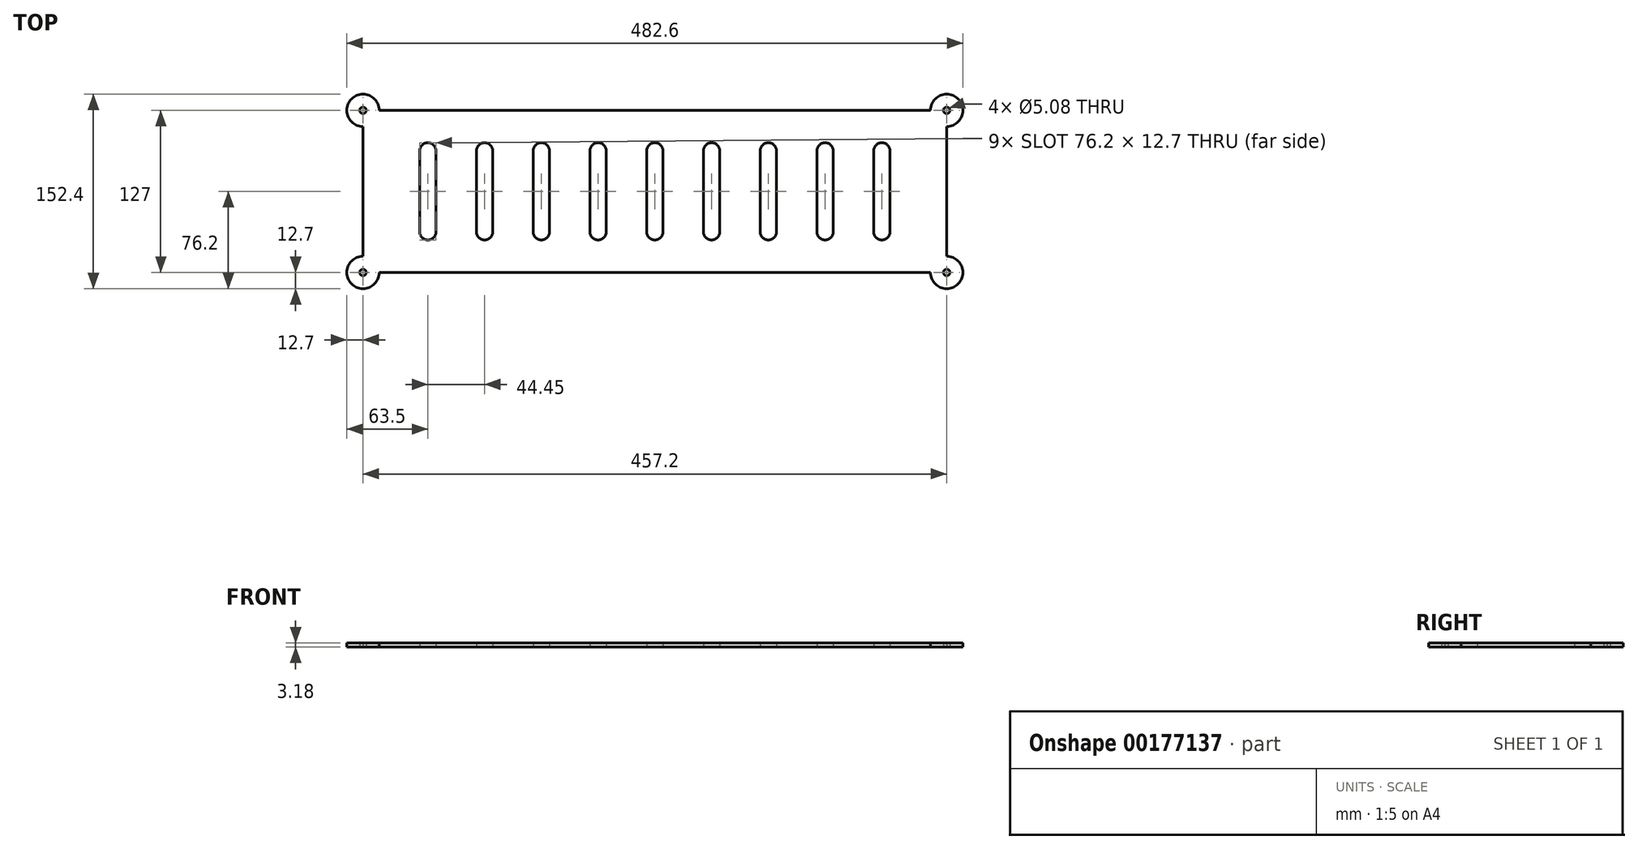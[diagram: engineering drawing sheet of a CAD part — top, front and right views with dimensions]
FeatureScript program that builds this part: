
annotation { "Feature Type Name" : "Feature", "Feature Type Description" : "" }
export const myFeature = defineFeature(function(context is Context, id is Id, definition is map)
    precondition{}
    {
        {
            var Q0;
            Q0=qCreatedBy(makeId("Top.planeOp"),FACE);
            var sketch = newSketch(context, id + "F0", { "sketchPlane" : qUnion([Q0])});
            skLineSegment(sketch, "E0.bottom", {"start": v(12.7, 0) * mm, "end": v(444.5, 0) * mm});
            skLineSegment(sketch, "E0.top", {"start": v(12.7, 127) * mm, "end": v(444.5, 127) * mm});
            skLineSegment(sketch, "E0.left", {"start": v(0, 12.7) * mm, "end": v(0, 114.3) * mm});
            skLineSegment(sketch, "E0.right", {"start": v(457.2, 12.7) * mm, "end": v(457.2, 114.3) * mm});
            skArc(sketch, "E1", {"start": v(457.2, 114.3) * mm, "mid": v(466.18, 135.98) * mm, "end": v(444.5, 127) * mm});
            skArc(sketch, "E2", {"start": v(444.5, 0) * mm, "mid": v(466.18, -8.98) * mm, "end": v(457.2, 12.7) * mm});
            skArc(sketch, "E3", {"start": v(0, 12.7) * mm, "mid": v(-8.98, -8.98) * mm, "end": v(12.7, 0) * mm});
            skArc(sketch, "E4", {"start": v(12.7, 127) * mm, "mid": v(-8.98, 135.98) * mm, "end": v(0, 114.3) * mm});
            skCircle(sketch, "E5", {"center": v(0, 127) * mm, "radius": 2.54 * mm});
            skCircle(sketch, "E6", {"center": v(0, 0) * mm, "radius": 2.54 * mm});
            skCircle(sketch, "E7", {"center": v(457.2, 127) * mm, "radius": 2.54 * mm});
            skCircle(sketch, "E8", {"center": v(457.2, 0) * mm, "radius": 2.54 * mm});
            skLineSegment(sketch, "E9", {"start": v(50.8, 31.75) * mm, "end": v(50.8, 95.25) * mm});
            skLineSegment(sketch, "E10", {"start": v(50.8, 95.25) * mm, "end": v(50.8, 127) * mm, "construction": true});
            skLineSegment(sketch, "E11", {"start": v(50.8, 31.75) * mm, "end": v(50.8, 0) * mm, "construction": true});
            skArc(sketch, "E12.0.startCap", {"start": v(57.15, 31.75) * mm, "mid": v(50.8, 25.4) * mm, "end": v(44.45, 31.75) * mm});
            skArc(sketch, "E12.0.endCap", {"start": v(44.45, 95.25) * mm, "mid": v(50.8, 101.6) * mm, "end": v(57.15, 95.25) * mm});
            skLineSegment(sketch, "E12.0.left", {"start": v(44.45, 31.75) * mm, "end": v(44.45, 95.25) * mm});
            skLineSegment(sketch, "E12.0.right", {"start": v(57.15, 31.75) * mm, "end": v(57.15, 95.25) * mm});
            skArc(sketch, "E13.1.0.0", {"start": v(88.9, 95.25) * mm, "mid": v(95.25, 101.6) * mm, "end": v(101.6, 95.25) * mm});
            skLineSegment(sketch, "E13.1.0.1", {"start": v(101.6, 31.75) * mm, "end": v(101.6, 95.25) * mm});
            skLineSegment(sketch, "E13.1.0.2", {"start": v(95.25, 31.75) * mm, "end": v(95.25, 95.25) * mm});
            skArc(sketch, "E13.1.0.3", {"start": v(101.6, 31.75) * mm, "mid": v(95.25, 25.4) * mm, "end": v(88.9, 31.75) * mm});
            skLineSegment(sketch, "E13.1.0.4", {"start": v(88.9, 31.75) * mm, "end": v(88.9, 95.25) * mm});
            skArc(sketch, "E13.2.0.0", {"start": v(133.35, 95.25) * mm, "mid": v(139.7, 101.6) * mm, "end": v(146.05, 95.25) * mm});
            skLineSegment(sketch, "E13.2.0.1", {"start": v(146.05, 31.75) * mm, "end": v(146.05, 95.25) * mm});
            skLineSegment(sketch, "E13.2.0.2", {"start": v(139.7, 31.75) * mm, "end": v(139.7, 95.25) * mm});
            skArc(sketch, "E13.2.0.3", {"start": v(146.05, 31.75) * mm, "mid": v(139.7, 25.4) * mm, "end": v(133.35, 31.75) * mm});
            skLineSegment(sketch, "E13.2.0.4", {"start": v(133.35, 31.75) * mm, "end": v(133.35, 95.25) * mm});
            skArc(sketch, "E13.3.0.0", {"start": v(177.8, 95.25) * mm, "mid": v(184.15, 101.6) * mm, "end": v(190.5, 95.25) * mm});
            skLineSegment(sketch, "E13.3.0.1", {"start": v(190.5, 31.75) * mm, "end": v(190.5, 95.25) * mm});
            skLineSegment(sketch, "E13.3.0.2", {"start": v(184.15, 31.75) * mm, "end": v(184.15, 95.25) * mm});
            skArc(sketch, "E13.3.0.3", {"start": v(190.5, 31.75) * mm, "mid": v(184.15, 25.4) * mm, "end": v(177.8, 31.75) * mm});
            skLineSegment(sketch, "E13.3.0.4", {"start": v(177.8, 31.75) * mm, "end": v(177.8, 95.25) * mm});
            skArc(sketch, "E13.4.0.0", {"start": v(222.25, 95.25) * mm, "mid": v(228.6, 101.6) * mm, "end": v(234.95, 95.25) * mm});
            skLineSegment(sketch, "E13.4.0.1", {"start": v(234.95, 31.75) * mm, "end": v(234.95, 95.25) * mm});
            skLineSegment(sketch, "E13.4.0.2", {"start": v(228.6, 31.75) * mm, "end": v(228.6, 95.25) * mm});
            skArc(sketch, "E13.4.0.3", {"start": v(234.95, 31.75) * mm, "mid": v(228.6, 25.4) * mm, "end": v(222.25, 31.75) * mm});
            skLineSegment(sketch, "E13.4.0.4", {"start": v(222.25, 31.75) * mm, "end": v(222.25, 95.25) * mm});
            skArc(sketch, "E13.5.0.0", {"start": v(266.7, 95.25) * mm, "mid": v(273.05, 101.6) * mm, "end": v(279.4, 95.25) * mm});
            skLineSegment(sketch, "E13.5.0.1", {"start": v(279.4, 31.75) * mm, "end": v(279.4, 95.25) * mm});
            skLineSegment(sketch, "E13.5.0.2", {"start": v(273.05, 31.75) * mm, "end": v(273.05, 95.25) * mm});
            skArc(sketch, "E13.5.0.3", {"start": v(279.4, 31.75) * mm, "mid": v(273.05, 25.4) * mm, "end": v(266.7, 31.75) * mm});
            skLineSegment(sketch, "E13.5.0.4", {"start": v(266.7, 31.75) * mm, "end": v(266.7, 95.25) * mm});
            skArc(sketch, "E13.6.0.0", {"start": v(311.15, 95.25) * mm, "mid": v(317.5, 101.6) * mm, "end": v(323.85, 95.25) * mm});
            skLineSegment(sketch, "E13.6.0.1", {"start": v(323.85, 31.75) * mm, "end": v(323.85, 95.25) * mm});
            skLineSegment(sketch, "E13.6.0.2", {"start": v(317.5, 31.75) * mm, "end": v(317.5, 95.25) * mm});
            skArc(sketch, "E13.6.0.3", {"start": v(323.85, 31.75) * mm, "mid": v(317.5, 25.4) * mm, "end": v(311.15, 31.75) * mm});
            skLineSegment(sketch, "E13.6.0.4", {"start": v(311.15, 31.75) * mm, "end": v(311.15, 95.25) * mm});
            skArc(sketch, "E13.7.0.0", {"start": v(355.6, 95.25) * mm, "mid": v(361.95, 101.6) * mm, "end": v(368.3, 95.25) * mm});
            skLineSegment(sketch, "E13.7.0.1", {"start": v(368.3, 31.75) * mm, "end": v(368.3, 95.25) * mm});
            skLineSegment(sketch, "E13.7.0.2", {"start": v(361.95, 31.75) * mm, "end": v(361.95, 95.25) * mm});
            skArc(sketch, "E13.7.0.3", {"start": v(368.3, 31.75) * mm, "mid": v(361.95, 25.4) * mm, "end": v(355.6, 31.75) * mm});
            skLineSegment(sketch, "E13.7.0.4", {"start": v(355.6, 31.75) * mm, "end": v(355.6, 95.25) * mm});
            skArc(sketch, "E13.8.0.0", {"start": v(400.05, 95.25) * mm, "mid": v(406.4, 101.6) * mm, "end": v(412.75, 95.25) * mm});
            skLineSegment(sketch, "E13.8.0.1", {"start": v(412.75, 31.75) * mm, "end": v(412.75, 95.25) * mm});
            skLineSegment(sketch, "E13.8.0.2", {"start": v(406.4, 31.75) * mm, "end": v(406.4, 95.25) * mm});
            skArc(sketch, "E13.8.0.3", {"start": v(412.75, 31.75) * mm, "mid": v(406.4, 25.4) * mm, "end": v(400.05, 31.75) * mm});
            skLineSegment(sketch, "E13.8.0.4", {"start": v(400.05, 31.75) * mm, "end": v(400.05, 95.25) * mm});
            skLineSegment(sketch, "E13.direction1", {"start": v(44.45, 31.75) * mm, "end": v(88.9, 31.75) * mm, "construction": true});
            skLineSegment(sketch, "E14", {"start": v(0, 63.5) * mm, "end": v(44.45, 63.5) * mm, "construction": true});
            skLineSegment(sketch, "E15", {"start": v(412.75, 63.5) * mm, "end": v(457.2, 63.5) * mm, "construction": true});
            skSolve(sketch);
        }
        {
            var Q0;
            Q0=makeQuery(id+"F0.imprint","IMPRINT",FACE,{"disambiguationData":[TD([[makeQuery(id+"F0.imprint","IMPRINT",EDGE,{"derivedFrom":sQuery(id+"F0.wireOp",EDGE,"E0.bottom")}),1.0]])]});
            extrude(context, id + "F1", {"entities" : qUnion([Q0]), "depth" : 3.17 * mm});
        }
    });
